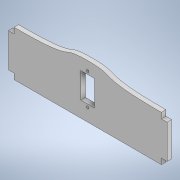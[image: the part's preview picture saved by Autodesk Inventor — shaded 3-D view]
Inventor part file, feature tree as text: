
AUTODESK INVENTOR PART (.ipt)
format: ipt  version: 2020.3 (Build 243373000, 373)  size: 140,800 bytes
history: native  units: mm
features: extrude x3, sketch x3
ambient origin geometry x8: Origin, YZ Plane, XZ Plane, XY Plane, X Axis, Y Axis, Z Axis, Center Point
bodies: Solid1 (feature_tree)
feature tree (6):
  extrude  "Extrusion1"  Depth=10.0mm TaperAngle=0.0deg
  sketch  "Sketch2"  dims[d8=0.0mm d9=0.0mm]
  extrude  "Extrusion2"  [1 undecoded]
  extrude  "Extrusion3"  [1 undecoded]
  sketch  "Sketch1"  dims[d4=4.0mm d5=0.0mm d6=10.0mm d7=0.0mm]
  sketch  "Sketch3"
note: 2 required parameter values undecoded (feature->parameter linkage not recoverable at this tier; creation-order binding heuristic only, values carry confidence <= 0.55)
